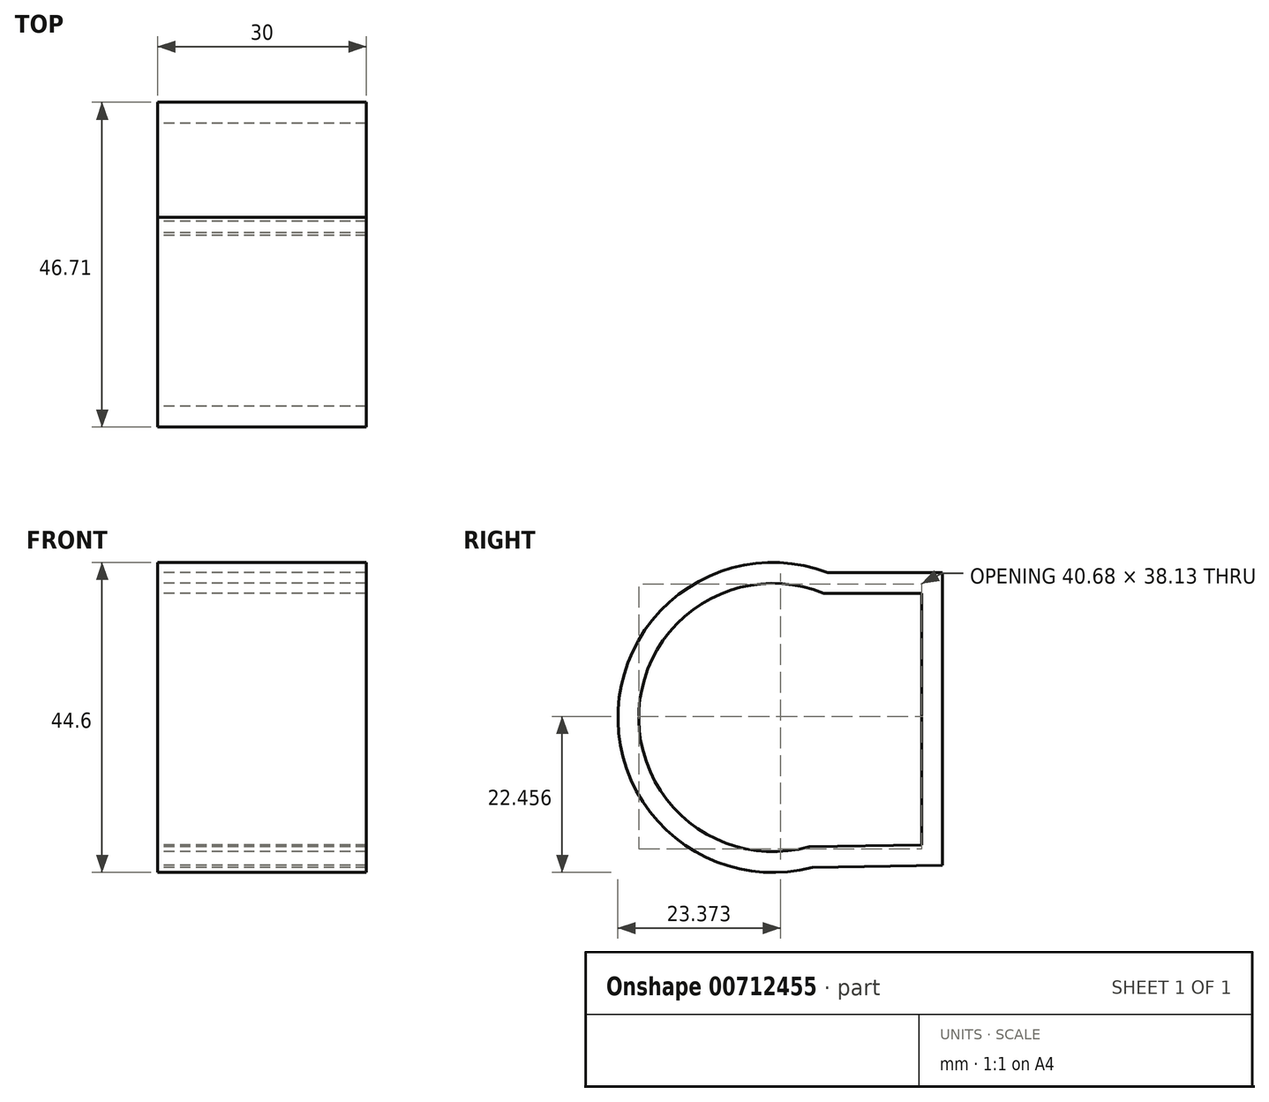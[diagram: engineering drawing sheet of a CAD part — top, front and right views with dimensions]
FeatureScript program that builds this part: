
annotation { "Feature Type Name" : "Feature", "Feature Type Description" : "" }
export const myFeature = defineFeature(function(context is Context, id is Id, definition is map)
    precondition{}
    {
        {
            var Q0;
            Q0=qCreatedBy(makeId("Right.planeOp"),FACE);
            var sketch = newSketch(context, id + "F0", { "sketchPlane" : qUnion([Q0])});
            skLineSegment(sketch, "E0.0", {"start": v(-53.23, 11.93) * mm, "end": v(-36.46, 12.19) * mm});
            skLineSegment(sketch, "E0.1", {"start": v(-36.46, 42.85) * mm, "end": v(-36.46, 12.19) * mm});
            skLineSegment(sketch, "E1.0", {"start": v(-50.56, 48.38) * mm, "end": v(-38.97, 48.38) * mm});
            skArc(sketch, "E1.1", {"start": v(-50.56, 48.38) * mm, "mid": v(-77.14, 31.48) * mm, "end": v(-52.37, 12.02) * mm});
            skLineSegment(sketch, "E2", {"start": v(-36.46, 42.85) * mm, "end": v(-36.46, 48.38) * mm});
            skLineSegment(sketch, "E3", {"start": v(-36.46, 48.38) * mm, "end": v(-38.97, 48.38) * mm});
            skSolve(sketch);
        }
        {
            var Q0;
            {var subQ4=sQuery(id+"F0.wireOp",EDGE,"E0.1");Q0=makeQuery(id+"F0.imprint","IMPRINT",FACE,{"disambiguationData":[TD([[makeQuery(id+"F0.imprint","IMPRINT",EDGE,{"derivedFrom":subQ4}),-1.0]])]});}
            extrude(context, id + "F1", {"entities" : qUnion([Q0]), "depth" : 30 * mm, "offsetDistance" : 25 * mm});
        }
        {
            var Q0;
            Q0=makeQuery(id+"F1.opExtrude","CAP_FACE",FACE,{"disambiguationData":[OSD([sQuery(id+"F0.wireOp",EDGE,"E0.0"),sQuery(id+"F0.wireOp",EDGE,"E0.1"),sQuery(id+"F0.wireOp",EDGE,"E1.0"),sQuery(id+"F0.wireOp",EDGE,"E1.1"),sQuery(id+"F0.wireOp",EDGE,"E2"),sQuery(id+"F0.wireOp",EDGE,"E3")])],"isStart":false});
            var Q1;
            Q1=makeQuery(id+"F1.opExtrude","CAP_FACE",FACE,{"disambiguationData":[OSD([sQuery(id+"F0.wireOp",EDGE,"E0.0"),sQuery(id+"F0.wireOp",EDGE,"E0.1"),sQuery(id+"F0.wireOp",EDGE,"E1.0"),sQuery(id+"F0.wireOp",EDGE,"E1.1"),sQuery(id+"F0.wireOp",EDGE,"E2"),sQuery(id+"F0.wireOp",EDGE,"E3")])],"isStart":true});
            shell(context, id + "F2", {"entities" : qUnion([Q0, Q1]), "thickness" : 3 * mm, "oppositeDirection" : true});
        }
    });
